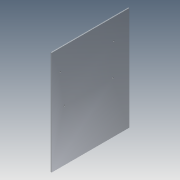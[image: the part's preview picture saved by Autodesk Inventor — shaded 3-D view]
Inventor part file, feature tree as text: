
AUTODESK INVENTOR PART (.ipt)
format: ipt  version: 2015 SP1 (Build 190203100, 203)  size: 101,888 bytes
history: native  units: mm
features: sketch x2, extrude x1, hole x1
ambient origin geometry x8: Origin, YZ Plane, XZ Plane, XY Plane, X Axis, Y Axis, Z Axis, Center Point
bodies: Solid1 (feature_tree)
feature tree (4):
  extrude  "Extrusion1"  Depth=120.0mm
  hole  "Hole1"  [1 undecoded]
  sketch  "Sketch1"  dims[d0=160.0mm d1=120.0mm]
  sketch  "Sketch2"  dims[d2=1.5mm d3=0.0mm d4=14.0mm d5=15.3mm d6=101.6mm d7=2.5mm d8=10.0mm d9=30.0mm d10=53.3mm d12=2.5mm d13=50.7mm d14=50.7mm d15=90.2mm d16=96.52mm d17=2.013mm d18=5.0mm d19=4.0mm d20=2.0mm d21=90.0deg d22=7.6mm d23=20.594885mm]
note: 1 required parameter value undecoded (feature->parameter linkage not recoverable at this tier; creation-order binding heuristic only, values carry confidence <= 0.55)
